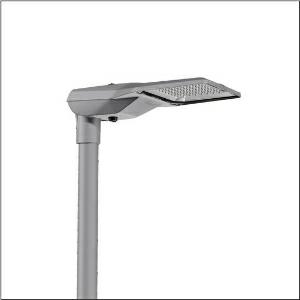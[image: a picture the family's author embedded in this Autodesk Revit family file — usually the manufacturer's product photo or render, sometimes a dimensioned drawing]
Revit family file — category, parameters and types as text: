
# Revit family: streetlight_sl_21_midi___p0_5a_5xe3v33t08mb_d4c3
name_source: partatom
category: Lighting Fixtures
units: mm (PartAtom-declared; Revit-internal decimal feet)

## family parameters
Cut with Voids When Loaded = No
Host = Face
Light Source = No
Part Type = Normal
Room Calculation Point = No
Round Connector Dimension = Use Diameter
Shared = No

## types (1)
- --- (1 x LED, 17960 lm, 136 W, 3000K)
    Apparent Load = 136 VA
    CIE Flux Codes = 37 73 96 100 100
    Color Rendering = 70
    Color Temperature = 3000K
    Default Elevation = 1800 mm
    Description = Streetlight SL 21 midi, mast luminaire, primary light control with lens, of PMMA, primary optical cover: cover, of toughened safety glass, transparent, light distribution: P0.5a, light emission: direct distribution, primary light characteristic: asymmetric, installation type: post-top, side-entry, LED, High Power LED, rated luminous flux: 17.960lm, luminous efficacy: 132lm/W, light colour: 730, colour temperature: 3000K, control gear: D4i, control: pre-setting: logarithmic dimming characteristic, flexible luminous flux parameterisation, time-dependent luminous flux control, constant luminous flux control, overheat protection, mains connection: 230..240V, AC, 50/60Hz, start of lifetime: 136W, end of service life: 142W, reduction: 61W, luminaire housing, of diecast aluminium, powder-coated, Siteco® metallic grey (DB 702S), corrosivity category C5 mid according to DIN EN ISO 12944, multi-level sealing system, sealing non-destructively replaceable, inclination adjustable: 0°, 5°, 10°, 15°, please order mast flange separately, length: 644mm, width: 335mm, height: 110mm, mast flange for spigot size: 42mm (side-entry): 5XC10008XM4, 60/48mm (side-entry/post-top): 5XC10108XM2, 76/60mm (side-entry/post-top): 5XC10108XM1, mounting height: 4..8m, Smart Interface below and above, protection rating (complete): IP66, insulation class (complete): insulation class II (safety insulation), certification: CE, ENEC, ENEC+, VDE, impact resistance: IK10, permissible operating ambient temperature for outdoor applications: -40..+50°C, standard-compliant lighting for roads and squares, packaging unit: 1 piece

Light Distribution: P0.5a
    Height = 111 mm
    Lamp = 1 x LED
    Lamp Light Flux = 17960 lm
    Lamp Power = 136 W
    Lamp count = 1
    Length = 644 mm
    Luminous efficacy = 132 lm/W
    Manufacturer = Siteco
    ModVariant = No
    Model = 5XE3V33T08MB
    Number of Poles = 1
    OnlyDefault = Yes
    Power Factor = 1
    Product Name = Streetlight SL 21 midi | P0.5a
    Product group = mast luminaire | pylon top
    ProductGroupID = 6100
    Protection Class = Protection class II
    Protection Degree = IP 66
    RLX_Detail_Level = 1
    RLX_Emergency_Light_Flux = 0 lm
    RLX_Emergency_Type = 0
    RLX_Emergency_Type_DB = No
    RlxData = <blob elided: 91001 chars, md5=c97fb2a7>
    Socket = socket
    Standby Power = 0 W
    System Light Flux = 17960 lm
    System Power = 136 W
    Type Comments = factory setting: luminous flux: 100 % | dim-lin: 254 | 695 mA
    Type Image = l_1004304.jpg
    URL = http://relux.com
    VarID = @adj_091399
    Voltage = 0 V
    Weight = 0.00 kg
    Width = 336 mm

## geometry (parser evidence)
native form markers: Blend x4, Sweep x11
no freeform markers — native parametric forms only
